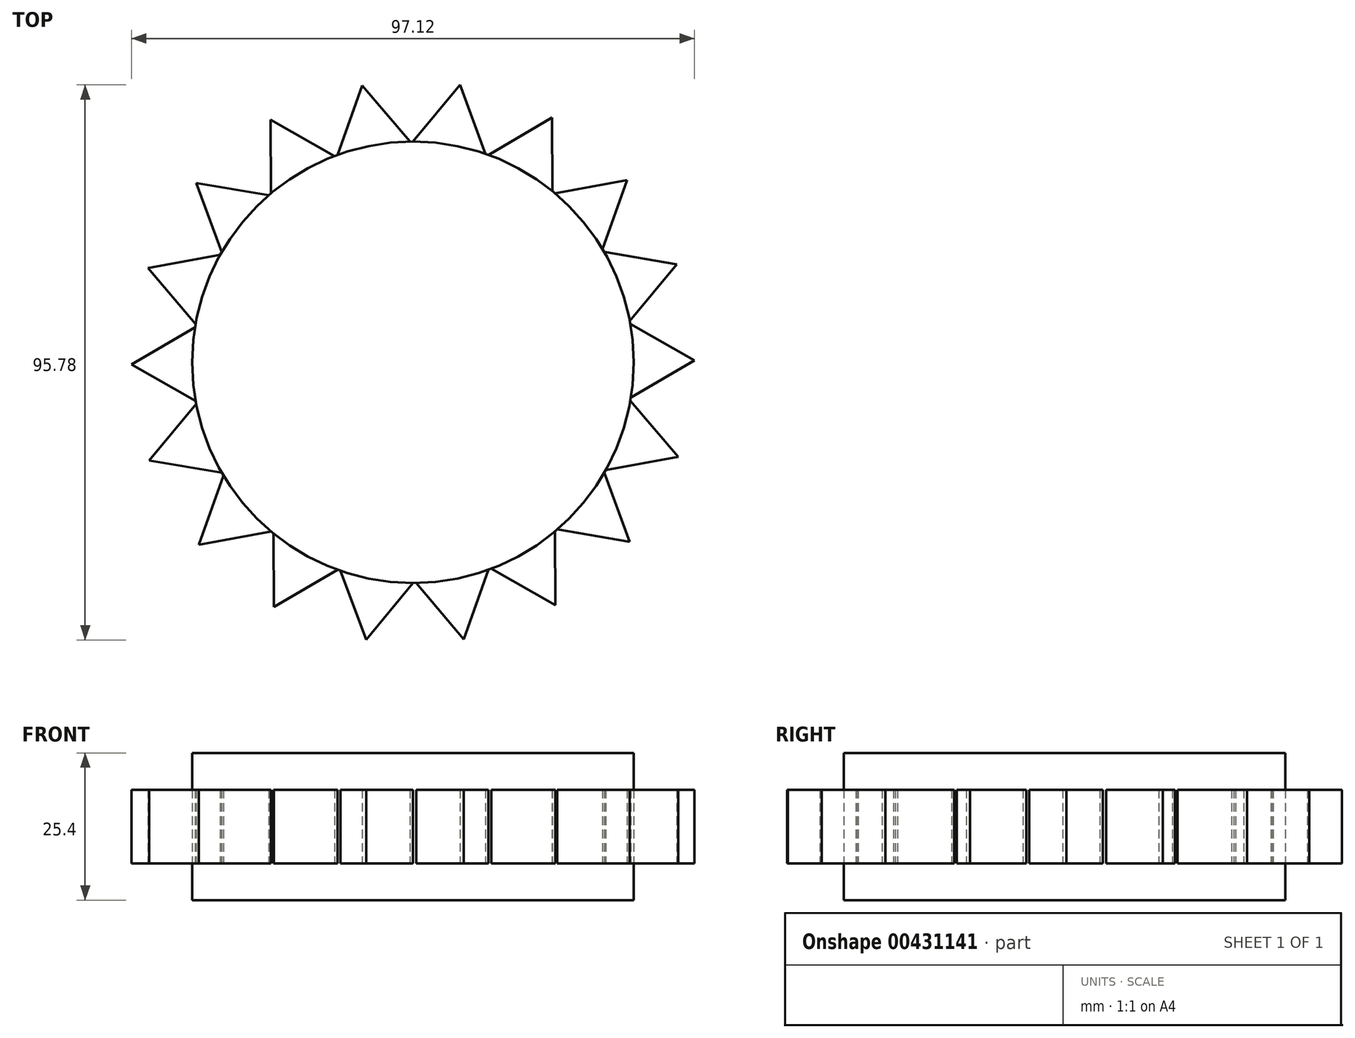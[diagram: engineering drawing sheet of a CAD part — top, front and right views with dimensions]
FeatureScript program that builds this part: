
annotation { "Feature Type Name" : "Feature", "Feature Type Description" : "" }
export const myFeature = defineFeature(function(context is Context, id is Id, definition is map)
    precondition{}
    {
        {
            var Q0;
            Q0=qCreatedBy(makeId("Top.planeOp"),FACE);
            var sketch = newSketch(context, id + "F0", { "sketchPlane" : qUnion([Q0])});
            skCircle(sketch, "E0", {"center": v(0, 0) * mm, "radius": 38.1 * mm});
            skLineSegment(sketch, "E1", {"start": v(0, 38.1) * mm, "end": v(8.1, 47.89) * mm});
            skLineSegment(sketch, "E2", {"start": v(8.1, 47.89) * mm, "end": v(12.52, 35.98) * mm});
            skLineSegment(sketch, "E3", {"start": v(0, 38.1) * mm, "end": v(12.52, 35.98) * mm});
            skSolve(sketch);
        }
        {
            var Q0;
            {var subQ0=sQuery(id+"F0.wireOp",EDGE,"E0");var subQ1=makeQuery(id+"F0.imprint","INTERSECT",VERTEX,{"derivedFrom":[subQ0,sQuery(id+"F0.wireOp",EDGE,"E1")]});Q0=makeQuery(id+"F0.imprint","IMPRINT",FACE,{"disambiguationData":[TD([[makeQuery(id+"F0.imprint","IMPRINT",EDGE,{"disambiguationData":[TD([[subQ1,1.0]])],"derivedFrom":subQ0}),1.0]])]});}
            var Q1;
            {var subQ0=sQuery(id+"F0.wireOp",EDGE,"E3");Q1=makeQuery(id+"F0.imprint","IMPRINT",FACE,{"disambiguationData":[TD([[makeQuery(id+"F0.imprint","IMPRINT",EDGE,{"derivedFrom":subQ0}),-1.0]])]});}
            extrude(context, id + "F1", {"entities" : qUnion([Q0, Q1]), "endBound" : BoundingType.SYMMETRIC, "depth" : 25.4 * mm});
        }
        {
            var Q0;
            {var subQ1=sQuery(id+"F0.wireOp",EDGE,"E1");Q0=makeQuery(id+"F0.imprint","IMPRINT",FACE,{"disambiguationData":[TD([[makeQuery(id+"F0.imprint","IMPRINT",EDGE,{"derivedFrom":subQ1}),-1.0]])]});}
            extrude(context, id + "F2", {"entities" : qUnion([Q0]), "endBound" : BoundingType.SYMMETRIC, "depth" : 12.7 * mm});
        }
        {
            var Q0;
            Q0=makeQuery(id+"F2.opExtrude","SWEPT_BODY",BODY,{"disambiguationData":[OSD([sQuery(id+"F0.wireOp",EDGE,"E0"),sQuery(id+"F0.wireOp",EDGE,"E1"),sQuery(id+"F0.wireOp",EDGE,"E2")])]});
            var Q1;
            Q1=makeQuery(id+"F1.opExtrude","CAP_EDGE",EDGE,{"disambiguationData":[OSD([sQuery(id+"F0.wireOp",EDGE,"E0")])],"isStart":false});
            circularPattern(context, id + "F3", {"entities" : qUnion([Q0]), "axis" : qUnion([Q1]), "angle" : 360 * degree, "instanceCount" : 18, "equalSpace" : true});
        }
    });
